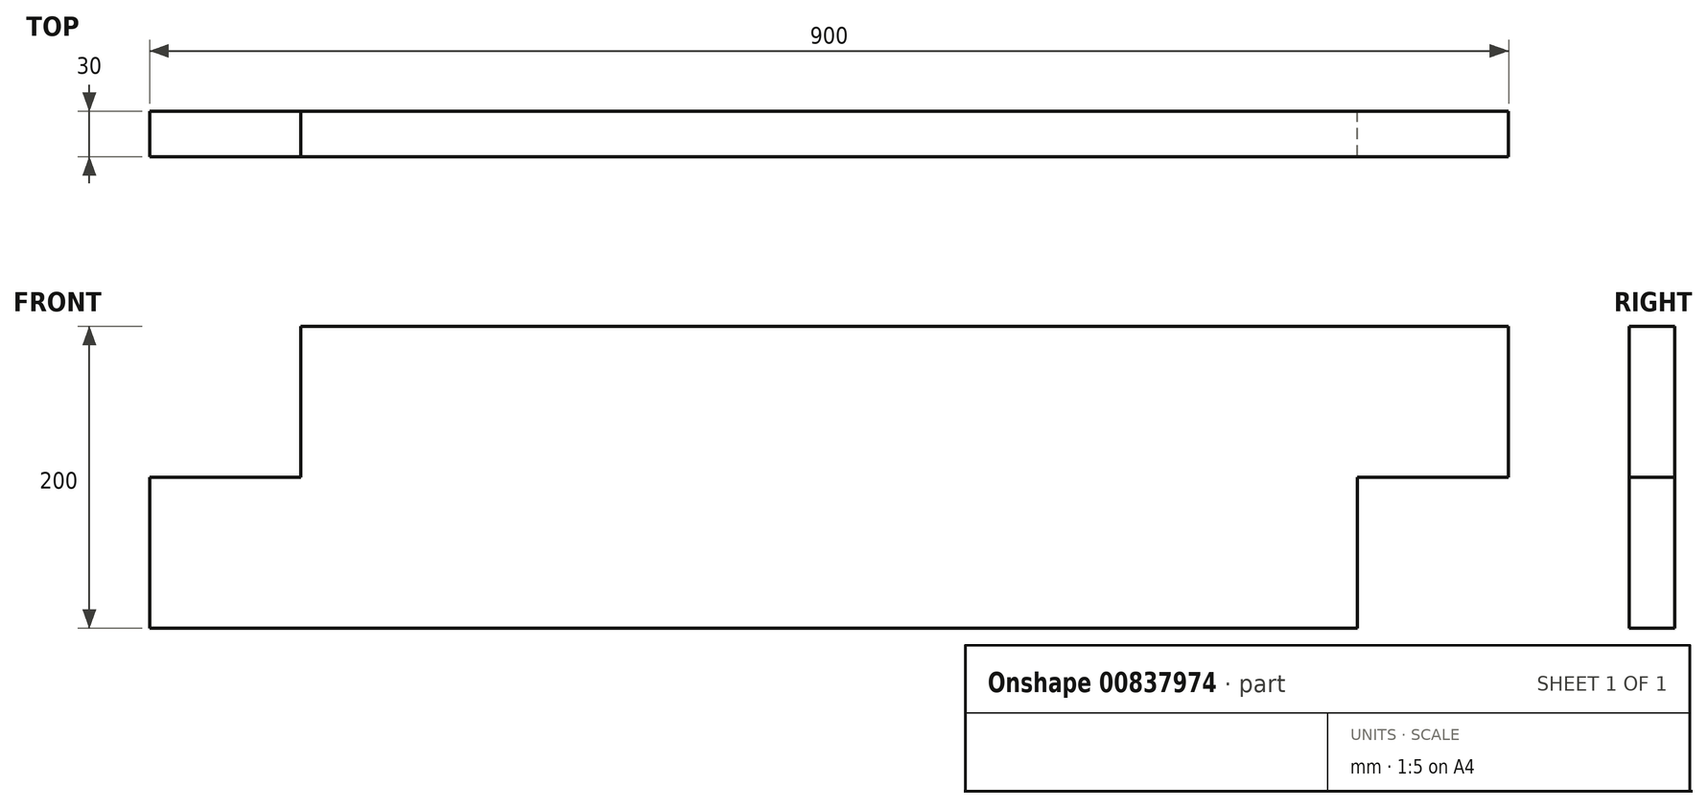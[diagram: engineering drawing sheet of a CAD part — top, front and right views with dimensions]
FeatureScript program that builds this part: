
annotation { "Feature Type Name" : "Feature", "Feature Type Description" : "" }
export const myFeature = defineFeature(function(context is Context, id is Id, definition is map)
    precondition{}
    {
        {
            var Q0;
            Q0=qCreatedBy(makeId("Front.planeOp"),FACE);
            var sketch = newSketch(context, id + "F0", { "sketchPlane" : qUnion([Q0])});
            skLineSegment(sketch, "E0", {"start": v(-204.24, -91.1) * mm, "end": v(-204.24, 8.9) * mm});
            skLineSegment(sketch, "E1", {"start": v(-204.24, 8.9) * mm, "end": v(-104.24, 8.9) * mm});
            skLineSegment(sketch, "E2", {"start": v(-104.24, 8.9) * mm, "end": v(-104.24, 108.9) * mm});
            skLineSegment(sketch, "E3", {"start": v(-104.24, 108.9) * mm, "end": v(695.76, 108.9) * mm});
            skLineSegment(sketch, "E4", {"start": v(695.76, 108.9) * mm, "end": v(695.76, 8.9) * mm});
            skLineSegment(sketch, "E5", {"start": v(695.76, 8.9) * mm, "end": v(595.76, 8.9) * mm});
            skLineSegment(sketch, "E6", {"start": v(595.76, 8.9) * mm, "end": v(595.76, -91.1) * mm});
            skLineSegment(sketch, "E7", {"start": v(595.76, -91.1) * mm, "end": v(-204.24, -91.1) * mm});
            skSolve(sketch);
        }
        {
            var Q0;
            Q0=makeQuery(id+"F0.imprint","IMPRINT",FACE,{"disambiguationData":[TD([[makeQuery(id+"F0.imprint","IMPRINT",EDGE,{"derivedFrom":sQuery(id+"F0.wireOp",EDGE,"E0")}),-1.0]])]});
            extrude(context, id + "F1", {"entities" : qUnion([Q0]), "depth" : 30 * mm, "offsetDistance" : 25 * mm});
        }
    });
